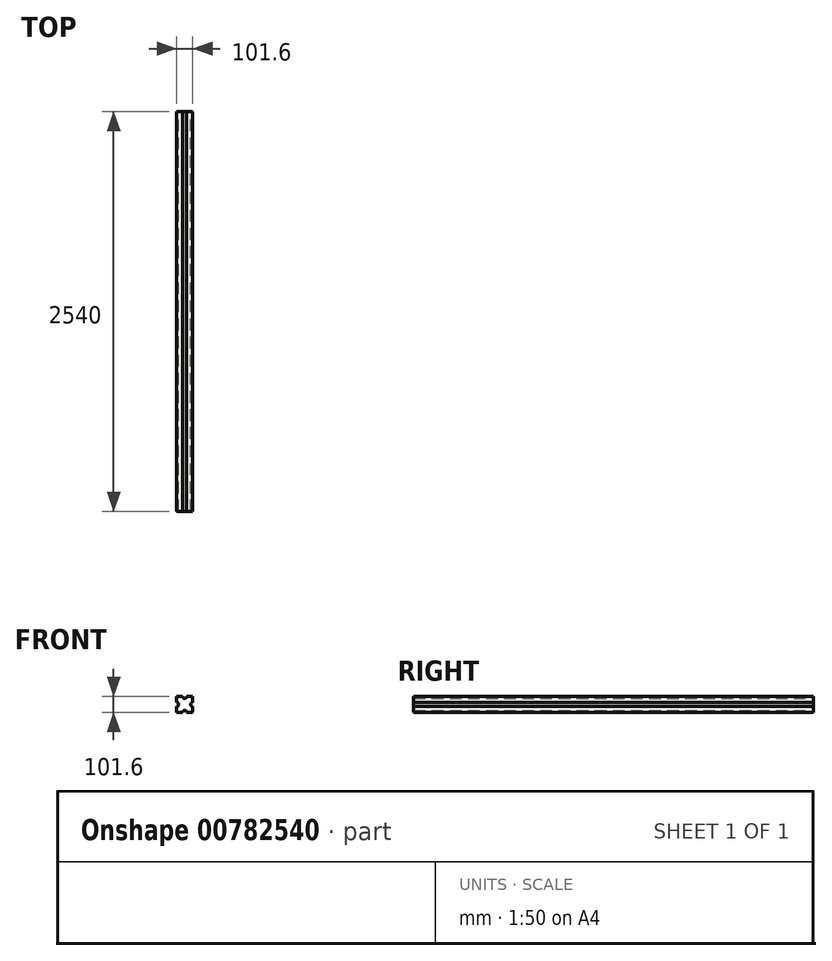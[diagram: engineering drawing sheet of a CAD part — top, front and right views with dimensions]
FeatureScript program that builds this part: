
annotation { "Feature Type Name" : "Feature", "Feature Type Description" : "" }
export const myFeature = defineFeature(function(context is Context, id is Id, definition is map)
    precondition{}
    {
        {
            var Q0;
            Q0=qCreatedBy(makeId("Front.planeOp"),FACE);
            var sketch = newSketch(context, id + "F0", { "sketchPlane" : qUnion([Q0])});
            skLineSegment(sketch, "E0.bottom", {"start": v(-50.8, -119.7) * mm, "end": v(-12.7, -119.7) * mm});
            skLineSegment(sketch, "E0.top", {"start": v(-50.8, -18.1) * mm, "end": v(-12.7, -18.1) * mm});
            skLineSegment(sketch, "E0.left", {"start": v(-50.8, -119.7) * mm, "end": v(-50.8, -81.6) * mm});
            skLineSegment(sketch, "E0.right", {"start": v(50.8, -119.7) * mm, "end": v(50.8, -81.6) * mm});
            skArc(sketch, "E1", {"start": v(50.8, -56.2) * mm, "mid": v(38.1, -68.9) * mm, "end": v(50.8, -81.6) * mm});
            skArc(sketch, "E2", {"start": v(12.7, -119.7) * mm, "mid": v(0, -107) * mm, "end": v(-12.7, -119.7) * mm});
            skLineSegment(sketch, "E3", {"start": v(38.1, -68.9) * mm, "end": v(-38.1, -68.9) * mm});
            skArc(sketch, "E4.MirrorC", {"start": v(12.7, -18.1) * mm, "mid": v(0, -30.8) * mm, "end": v(-12.7, -18.1) * mm});
            skLineSegment(sketch, "E5", {"start": v(0, -30.8) * mm, "end": v(0, -107) * mm});
            skArc(sketch, "E6.MirrorC", {"start": v(-50.8, -56.2) * mm, "mid": v(-38.1, -68.9) * mm, "end": v(-50.8, -81.6) * mm});
            skLineSegment(sketch, "E7.trimOffspring", {"start": v(12.7, -18.1) * mm, "end": v(50.8, -18.1) * mm});
            skLineSegment(sketch, "E8.trimOffspring", {"start": v(-50.8, -56.2) * mm, "end": v(-50.8, -18.1) * mm});
            skLineSegment(sketch, "E9.trimOffspring", {"start": v(12.7, -119.7) * mm, "end": v(50.8, -119.7) * mm});
            skLineSegment(sketch, "E10.trimOffspring", {"start": v(50.8, -56.2) * mm, "end": v(50.8, -18.1) * mm});
            skSolve(sketch);
        }
        {
            var Q0;
            {var subQ6=sQuery(id+"F0.wireOp",EDGE,"E0.bottom");Q0=makeQuery(id+"F0.imprint","IMPRINT",FACE,{"disambiguationData":[TD([[makeQuery(id+"F0.imprint","IMPRINT",EDGE,{"derivedFrom":subQ6}),1.0]])]});}
            var Q1;
            {var subQ5=sQuery(id+"F0.wireOp",EDGE,"E0.right");Q1=makeQuery(id+"F0.imprint","IMPRINT",FACE,{"disambiguationData":[TD([[makeQuery(id+"F0.imprint","IMPRINT",EDGE,{"derivedFrom":subQ5}),1.0]])]});}
            var Q2;
            {var subQ5=sQuery(id+"F0.wireOp",EDGE,"E0.top");Q2=makeQuery(id+"F0.imprint","IMPRINT",FACE,{"disambiguationData":[TD([[makeQuery(id+"F0.imprint","IMPRINT",EDGE,{"derivedFrom":subQ5}),-1.0]])]});}
            var Q3;
            {var subQ5=sQuery(id+"F0.wireOp",EDGE,"E7.trimOffspring");Q3=makeQuery(id+"F0.imprint","IMPRINT",FACE,{"disambiguationData":[TD([[makeQuery(id+"F0.imprint","IMPRINT",EDGE,{"derivedFrom":subQ5}),-1.0]])]});}
            extrude(context, id + "F1", {"entities" : qUnion([Q0, Q1, Q2, Q3]), "depth" : 2540 * mm, "offsetDistance" : 25.4 * mm});
        }
    });
